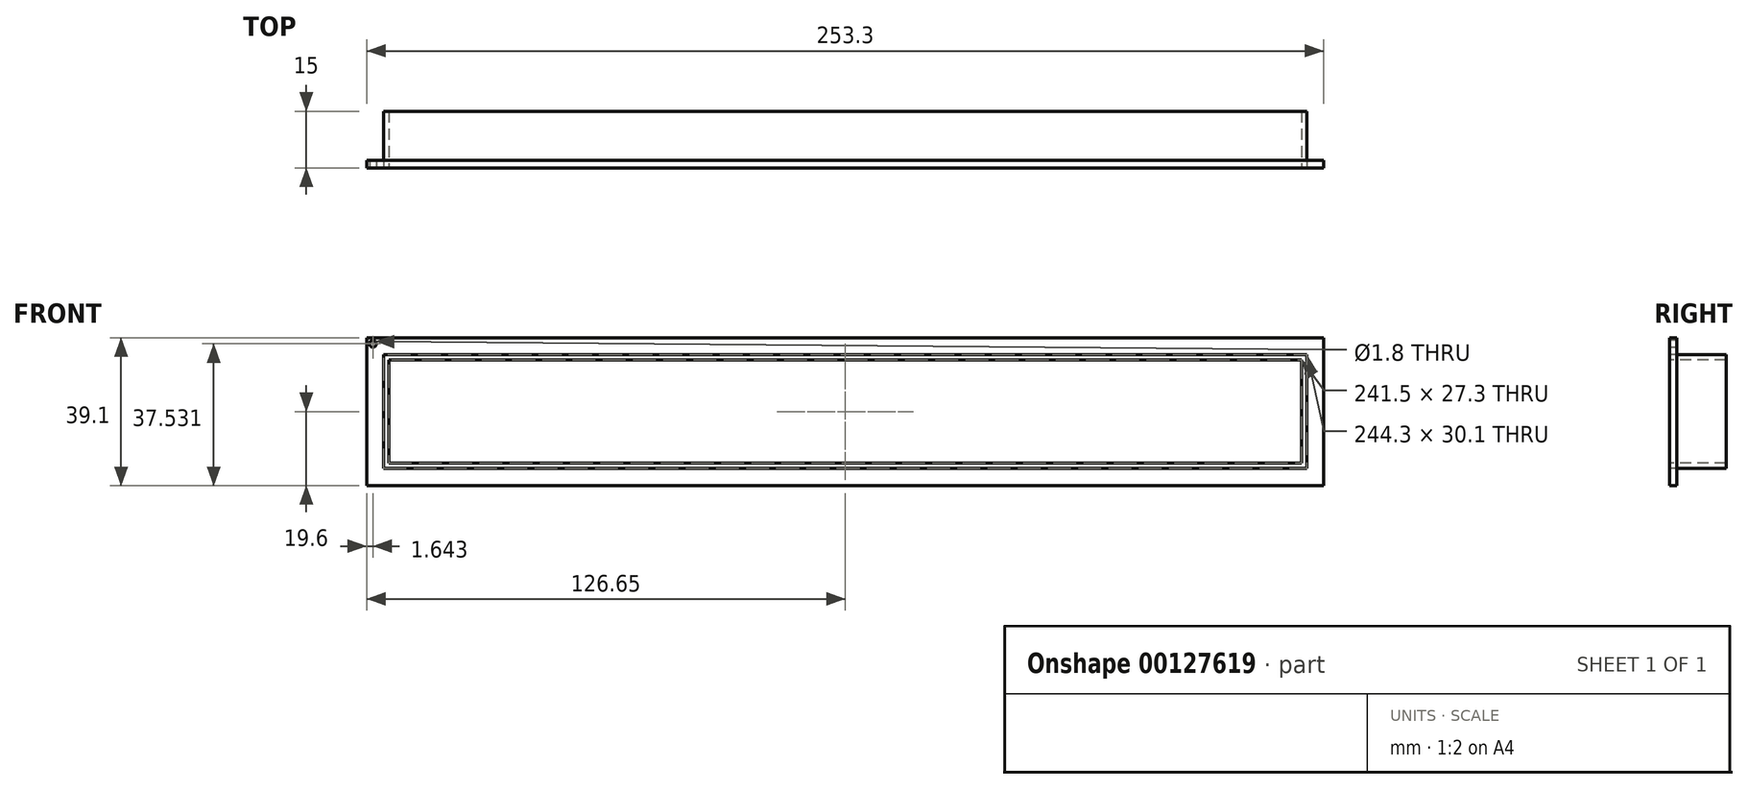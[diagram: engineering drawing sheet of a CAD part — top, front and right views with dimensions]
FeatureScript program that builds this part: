
annotation { "Feature Type Name" : "Feature", "Feature Type Description" : "" }
export const myFeature = defineFeature(function(context is Context, id is Id, definition is map)
    precondition{}
    {
        {
            var Q0;
            Q0=qCreatedBy(makeId("Front.planeOp"),FACE);
            var sketch = newSketch(context, id + "F0", { "sketchPlane" : qUnion([Q0])});
            skLineSegment(sketch, "E0.bottom", {"start": v(-126.65, 19.5) * mm, "end": v(126.65, 19.5) * mm});
            skLineSegment(sketch, "E0.top", {"start": v(-126.65, -19.6) * mm, "end": v(126.65, -19.6) * mm});
            skLineSegment(sketch, "E0.left", {"start": v(-126.65, 19.5) * mm, "end": v(-126.65, -19.6) * mm});
            skLineSegment(sketch, "E0.right", {"start": v(126.65, 19.5) * mm, "end": v(126.65, -19.6) * mm});
            skLineSegment(sketch, "E1", {"start": v(0, -55.17) * mm, "end": v(0, 70.33) * mm, "construction": true});
            skLineSegment(sketch, "E2", {"start": v(-73, 0) * mm, "end": v(60.08, 0) * mm, "construction": true});
            skSolve(sketch);
        }
        {
            var Q0;
            Q0=makeQuery(id+"F0.imprint","IMPRINT",FACE,{"disambiguationData":[TD([[makeQuery(id+"F0.imprint","IMPRINT",EDGE,{"derivedFrom":sQuery(id+"F0.wireOp",EDGE,"E0.bottom")}),-1.0]])]});
            extrude(context, id + "F1", {"entities" : qUnion([Q0]), "endBound" : BoundingType.SYMMETRIC, "depth" : 2 * mm});
        }
        {
            var Q0;
            Q0=makeQuery(id+"F1.opExtrude","CAP_FACE",FACE,{"disambiguationData":[OSD([sQuery(id+"F0.wireOp",EDGE,"E0.bottom"),sQuery(id+"F0.wireOp",EDGE,"E0.top"),sQuery(id+"F0.wireOp",EDGE,"E0.left"),sQuery(id+"F0.wireOp",EDGE,"E0.right")])],"isStart":false});
            var sketch = newSketch(context, id + "F2", { "sketchPlane" : qUnion([Q0])});
            skLineSegment(sketch, "E3.bottom", {"start": v(-122.15, 15.05) * mm, "end": v(122.15, 15.05) * mm});
            skLineSegment(sketch, "E3.top", {"start": v(-122.15, -15.05) * mm, "end": v(122.15, -15.05) * mm});
            skLineSegment(sketch, "E3.left", {"start": v(-122.15, 15.05) * mm, "end": v(-122.15, -15.05) * mm});
            skLineSegment(sketch, "E3.right", {"start": v(122.15, 15.05) * mm, "end": v(122.15, -15.05) * mm});
            skLineSegment(sketch, "E4", {"start": v(0, 70.05) * mm, "end": v(0, -51.52) * mm, "construction": true});
            skLineSegment(sketch, "E5", {"start": v(0, 0) * mm, "end": v(-153, 0) * mm, "construction": true});
            skLineSegment(sketch, "E6", {"start": v(-153, 0) * mm, "end": v(142.9, 0) * mm, "construction": true});
            skSolve(sketch);
        }
        {
            var Q0;
            Q0 = qSketchRegion(id + "F2", true);
            extrude(context, id + "F3", {"entities" : qUnion([Q0]), "operationType" : NewBodyOperationType.REMOVE, "endBound" : BoundingType.THROUGH_ALL, "oppositeDirection" : true, "depth" : 25 * mm});
        }
        {
            var Q0;
            Q0=makeQuery(id+"F1.opExtrude","CAP_FACE",FACE,{"disambiguationData":[OSD([sQuery(id+"F0.wireOp",EDGE,"E0.bottom"),sQuery(id+"F0.wireOp",EDGE,"E0.top"),sQuery(id+"F0.wireOp",EDGE,"E0.left"),sQuery(id+"F0.wireOp",EDGE,"E0.right")])],"isStart":false});
            var sketch = newSketch(context, id + "F4", { "sketchPlane" : qUnion([Q0])});
            skLineSegment(sketch, "E7.bottom", {"start": v(-122.15, 15.05) * mm, "end": v(122.15, 15.05) * mm});
            skLineSegment(sketch, "E7.top", {"start": v(-122.15, -15.05) * mm, "end": v(122.15, -15.05) * mm});
            skLineSegment(sketch, "E7.left", {"start": v(-122.15, 15.05) * mm, "end": v(-122.15, -15.05) * mm});
            skLineSegment(sketch, "E7.right", {"start": v(122.15, 15.05) * mm, "end": v(122.15, -15.05) * mm});
            skLineSegment(sketch, "E8.bottom", {"start": v(-120.75, 13.65) * mm, "end": v(120.75, 13.65) * mm});
            skLineSegment(sketch, "E8.top", {"start": v(-120.75, -13.65) * mm, "end": v(120.75, -13.65) * mm});
            skLineSegment(sketch, "E8.left", {"start": v(-120.75, 13.65) * mm, "end": v(-120.75, -13.65) * mm});
            skLineSegment(sketch, "E8.right", {"start": v(120.75, 13.65) * mm, "end": v(120.75, -13.65) * mm});
            skSolve(sketch);
        }
        {
            var Q0;
            Q0 = qSketchRegion(id + "F4", true);
            extrude(context, id + "F5", {"entities" : qUnion([Q0]), "oppositeDirection" : true, "depth" : 15 * mm});
        }
        {
            var Q0;
            Q0=makeQuery(id+"F1.opExtrude","CAP_FACE",FACE,{"disambiguationData":[OSD([sQuery(id+"F0.wireOp",EDGE,"E0.bottom"),sQuery(id+"F0.wireOp",EDGE,"E0.top"),sQuery(id+"F0.wireOp",EDGE,"E0.left"),sQuery(id+"F0.wireOp",EDGE,"E0.right")])],"isStart":false});
            var sketch = newSketch(context, id + "F6", { "sketchPlane" : qUnion([Q0])});
            skSolve(sketch);
        }
        {
            var Q0;
            Q0=makeQuery(id+"F6.imprint","IMPRINT",FACE,{"disambiguationData":[TD([[makeQuery(id+"F6.imprint","IMPRINT",EDGE,{"derivedFrom":makeQuery(id+"F1.opExtrude","CAP_EDGE",EDGE,{"disambiguationData":[OSD([sQuery(id+"F0.wireOp",EDGE,"E0.bottom")])],"isStart":false})}),-1.0]])]});
            var sketch = newSketch(context, id + "F7", { "sketchPlane" : qUnion([Q0])});
            skCircle(sketch, "E9", {"center": v(-30.68, 17.08) * mm, "radius": 1.35 * mm});
            skSolve(sketch);
        }
        {
            var Q0;
            Q0=makeQuery(id+"F6.imprint","IMPRINT",FACE,{"disambiguationData":[TD([[makeQuery(id+"F6.imprint","IMPRINT",EDGE,{"derivedFrom":makeQuery(id+"F1.opExtrude","CAP_EDGE",EDGE,{"disambiguationData":[OSD([sQuery(id+"F0.wireOp",EDGE,"E0.bottom")])],"isStart":false})}),-1.0]])]});
            var sketch = newSketch(context, id + "F8", { "sketchPlane" : qUnion([Q0])});
            skCircle(sketch, "E10", {"center": v(-125, 17.93) * mm, "radius": 0.9 * mm});
            skSolve(sketch);
        }
        {
            var Q0;
            Q0 = qSketchRegion(id + "F8", true);
            extrude(context, id + "F9", {"entities" : qUnion([Q0]), "operationType" : NewBodyOperationType.REMOVE, "oppositeDirection" : true, "depth" : 50 * mm});
        }
    });
